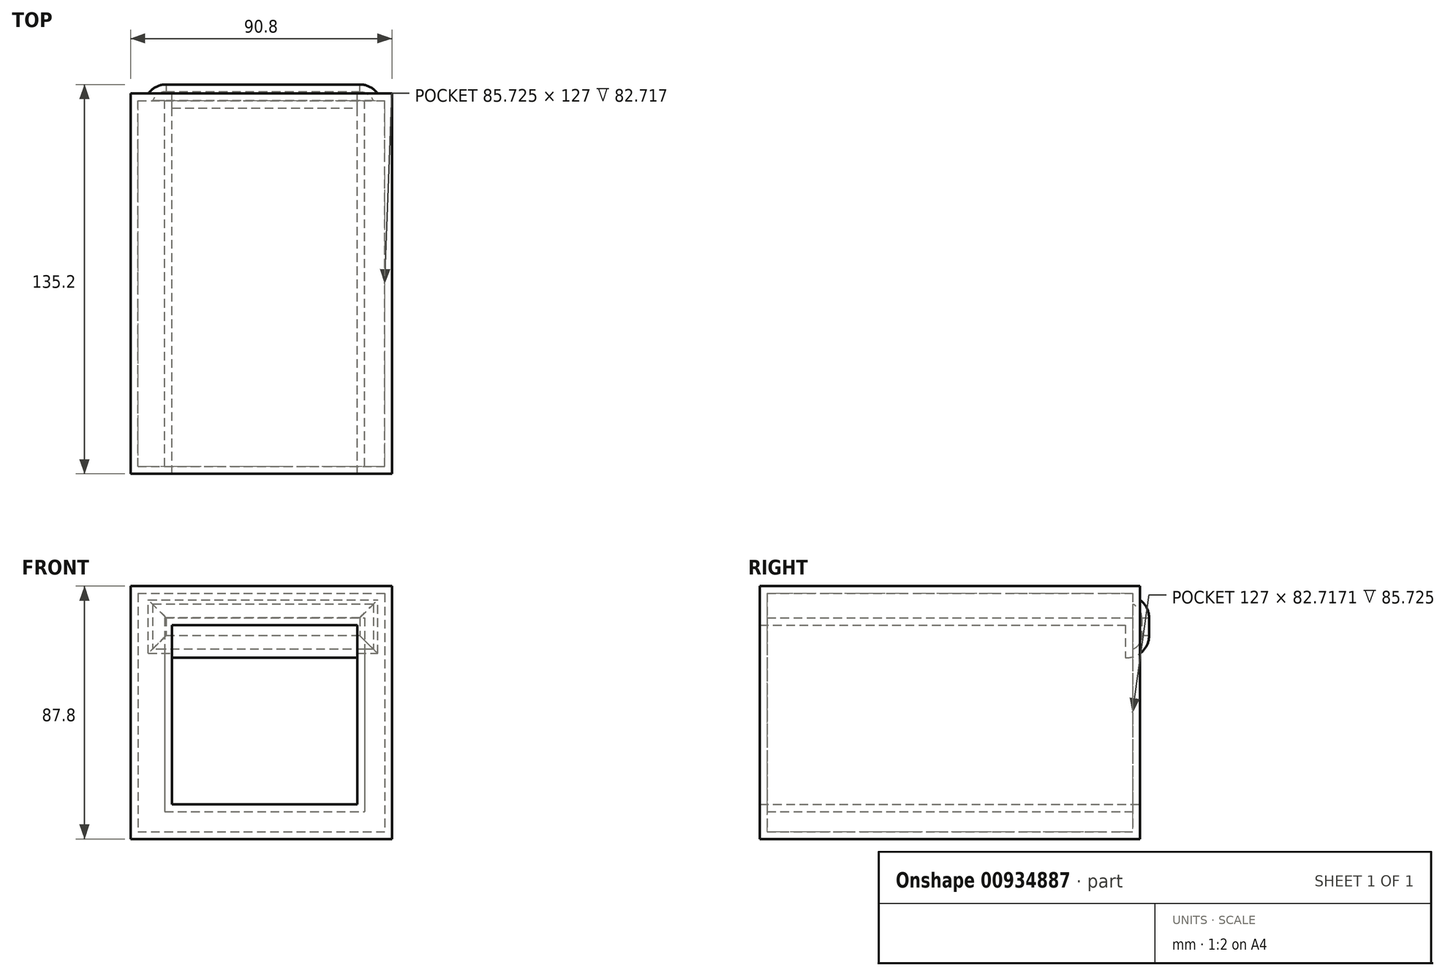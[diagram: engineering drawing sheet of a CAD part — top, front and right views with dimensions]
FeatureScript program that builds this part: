
annotation { "Feature Type Name" : "Feature", "Feature Type Description" : "" }
export const myFeature = defineFeature(function(context is Context, id is Id, definition is map)
    precondition{}
    {
        {
            var Q0;
            Q0=qCreatedBy(makeId("Front.planeOp"),FACE);
            var sketch = newSketch(context, id + "F0", { "sketchPlane" : qUnion([Q0])});
            skLineSegment(sketch, "E0.bottom", {"start": v(-42.86, 53.09) * mm, "end": v(-33.54, 53.09) * mm});
            skLineSegment(sketch, "E0.top", {"start": v(-42.86, -29.63) * mm, "end": v(-33.54, -29.63) * mm});
            skLineSegment(sketch, "E0.left", {"start": v(-42.86, 53.09) * mm, "end": v(-42.86, -29.63) * mm});
            skLineSegment(sketch, "E0.right", {"start": v(-33.54, 53.09) * mm, "end": v(-33.54, -29.63) * mm});
            skLineSegment(sketch, "E1.bottom", {"start": v(-33.54, 53.09) * mm, "end": v(35.94, 53.09) * mm});
            skLineSegment(sketch, "E1.top", {"start": v(-33.54, 44.67) * mm, "end": v(35.94, 44.67) * mm});
            skLineSegment(sketch, "E1.left", {"start": v(-33.54, 53.09) * mm, "end": v(-33.54, 44.67) * mm});
            skLineSegment(sketch, "E1.right", {"start": v(35.94, 53.09) * mm, "end": v(35.94, 44.67) * mm});
            skLineSegment(sketch, "E2.top", {"start": v(-33.54, -29.63) * mm, "end": v(35.94, -29.63) * mm});
            skLineSegment(sketch, "E2.left", {"start": v(-33.54, 44.67) * mm, "end": v(-33.54, -29.63) * mm});
            skLineSegment(sketch, "E2.right", {"start": v(35.94, 44.67) * mm, "end": v(35.94, -29.63) * mm});
            skLineSegment(sketch, "E3.bottom", {"start": v(35.94, 53.09) * mm, "end": v(42.86, 53.09) * mm});
            skLineSegment(sketch, "E3.top", {"start": v(35.94, -29.63) * mm, "end": v(42.86, -29.63) * mm});
            skLineSegment(sketch, "E3.left", {"start": v(35.94, 53.09) * mm, "end": v(35.94, -29.63) * mm});
            skLineSegment(sketch, "E3.right", {"start": v(42.86, 53.09) * mm, "end": v(42.86, -29.63) * mm});
            skLineSegment(sketch, "E4.top", {"start": v(-33.54, -22.7) * mm, "end": v(35.94, -22.7) * mm});
            skLineSegment(sketch, "E4.left", {"start": v(-33.54, -29.63) * mm, "end": v(-33.54, -22.7) * mm});
            skLineSegment(sketch, "E4.right", {"start": v(35.94, -29.63) * mm, "end": v(35.94, -22.7) * mm});
            skSolve(sketch);
        }
        {
            var Q0;
            {var subQ4=sQuery(id+"F0.wireOp",EDGE,"E0.bottom");Q0=makeQuery(id+"F0.imprint","IMPRINT",FACE,{"disambiguationData":[TD([[makeQuery(id+"F0.imprint","IMPRINT",EDGE,{"derivedFrom":subQ4}),-1.0]])]});}
            var Q1;
            {var subQ3=sQuery(id+"F0.wireOp",EDGE,"E1.right");Q1=makeQuery(id+"F0.imprint","IMPRINT",FACE,{"disambiguationData":[TD([[makeQuery(id+"F0.imprint","IMPRINT",EDGE,{"derivedFrom":subQ3}),1.0]])]});}
            var Q2;
            {var subQ0=sQuery(id+"F0.wireOp",EDGE,"E1.bottom");Q2=makeQuery(id+"F0.imprint","IMPRINT",FACE,{"disambiguationData":[TD([[makeQuery(id+"F0.imprint","IMPRINT",EDGE,{"derivedFrom":subQ0}),-1.0]])]});}
            var Q3;
            {var subQ0=sQuery(id+"F0.wireOp",EDGE,"E2.top");Q3=makeQuery(id+"F0.imprint","IMPRINT",FACE,{"disambiguationData":[TD([[makeQuery(id+"F0.imprint","IMPRINT",EDGE,{"derivedFrom":subQ0}),1.0]])]});}
            extrude(context, id + "F1", {"entities" : qUnion([Q0, Q1, Q2, Q3]), "depth" : 127 * mm, "offsetDistance" : 25.4 * mm});
        }
        {
            var Q0;
            {var subQ0=sQuery(id+"F0.wireOp",EDGE,"E1.top");Q0=makeQuery(id+"F0.imprint","IMPRINT",FACE,{"disambiguationData":[TD([[makeQuery(id+"F0.imprint","IMPRINT",EDGE,{"derivedFrom":subQ0}),-1.0]])]});}
            extrude(context, id + "F2", {"entities" : qUnion([Q0]), "operationType" : NewBodyOperationType.REMOVE, "oppositeDirection" : true, "depth" : 25.4 * mm, "offsetDistance" : 25.4 * mm});
        }
        {
            var Q0;
            Q0=makeQuery(id+"F1.opExtrude","CAP_FACE",FACE,{"disambiguationData":[OSD([sQuery(id+"F0.wireOp",EDGE,"E0.bottom"),sQuery(id+"F0.wireOp",EDGE,"E0.top"),sQuery(id+"F0.wireOp",EDGE,"E0.left"),sQuery(id+"F0.wireOp",EDGE,"E0.right"),sQuery(id+"F0.wireOp",EDGE,"E1.bottom"),sQuery(id+"F0.wireOp",EDGE,"E1.top"),sQuery(id+"F0.wireOp",EDGE,"E2.top"),sQuery(id+"F0.wireOp",EDGE,"E2.right"),sQuery(id+"F0.wireOp",EDGE,"E3.bottom"),sQuery(id+"F0.wireOp",EDGE,"E3.top"),sQuery(id+"F0.wireOp",EDGE,"E3.right"),sQuery(id+"F0.wireOp",EDGE,"E4.top")])],"isStart":true});
            var sketch = newSketch(context, id + "F3", { "sketchPlane" : qUnion([Q0])});
            skLineSegment(sketch, "E5.bottom", {"start": v(-38.98, 49.36) * mm, "end": v(37.77, 49.36) * mm});
            skLineSegment(sketch, "E5.top", {"start": v(-38.98, 33.7) * mm, "end": v(37.77, 33.7) * mm});
            skLineSegment(sketch, "E5.left", {"start": v(-38.98, 49.36) * mm, "end": v(-38.98, 33.7) * mm});
            skLineSegment(sketch, "E5.right", {"start": v(37.77, 49.36) * mm, "end": v(37.77, 33.7) * mm});
            skSolve(sketch);
        }
        {
            var Q0;
            Q0 = qSketchRegion(id + "F3", true);
            extrude(context, id + "F4", {"entities" : qUnion([Q0]), "operationType" : NewBodyOperationType.ADD, "depth" : 3.12 * mm, "offsetDistance" : 25.4 * mm});
        }
        {
            var Q0;
            Q0=makeQuery(id+"F4.opExtrude","CAP_EDGE",EDGE,{"disambiguationData":[OSD([sQuery(id+"F3.wireOp",EDGE,"E5.bottom")])],"isStart":false});
            var Q1;
            Q1=makeQuery(id+"F4.opExtrude","CAP_EDGE",EDGE,{"disambiguationData":[OSD([sQuery(id+"F3.wireOp",EDGE,"E5.left")])],"isStart":false});
            var Q2;
            Q2=makeQuery(id+"F4.opExtrude","CAP_EDGE",EDGE,{"disambiguationData":[OSD([sQuery(id+"F3.wireOp",EDGE,"E5.top")])],"isStart":false});
            var Q3;
            Q3=makeQuery(id+"F4.opExtrude","CAP_EDGE",EDGE,{"disambiguationData":[OSD([sQuery(id+"F3.wireOp",EDGE,"E5.right")])],"isStart":false});
            fillet(context, id + "F5", {"entities" : qUnion([Q0, Q1, Q2, Q3]), "radius" : 5.08 * mm, "tangentPropagation" : true, "allowEdgeOverflow" : false});
        }
        {
            var Q0;
            Q0=makeQuery(id+"F4.opExtrude","CAP_FACE",FACE,{"disambiguationData":[OSD([sQuery(id+"F3.wireOp",EDGE,"E5.bottom"),sQuery(id+"F3.wireOp",EDGE,"E5.top"),sQuery(id+"F3.wireOp",EDGE,"E5.left"),sQuery(id+"F3.wireOp",EDGE,"E5.right")])],"isStart":false});
            shell(context, id + "F6", {"entities" : qUnion([Q0]), "thickness" : 2.54 * mm, "oppositeDirection" : true});
        }
    });
